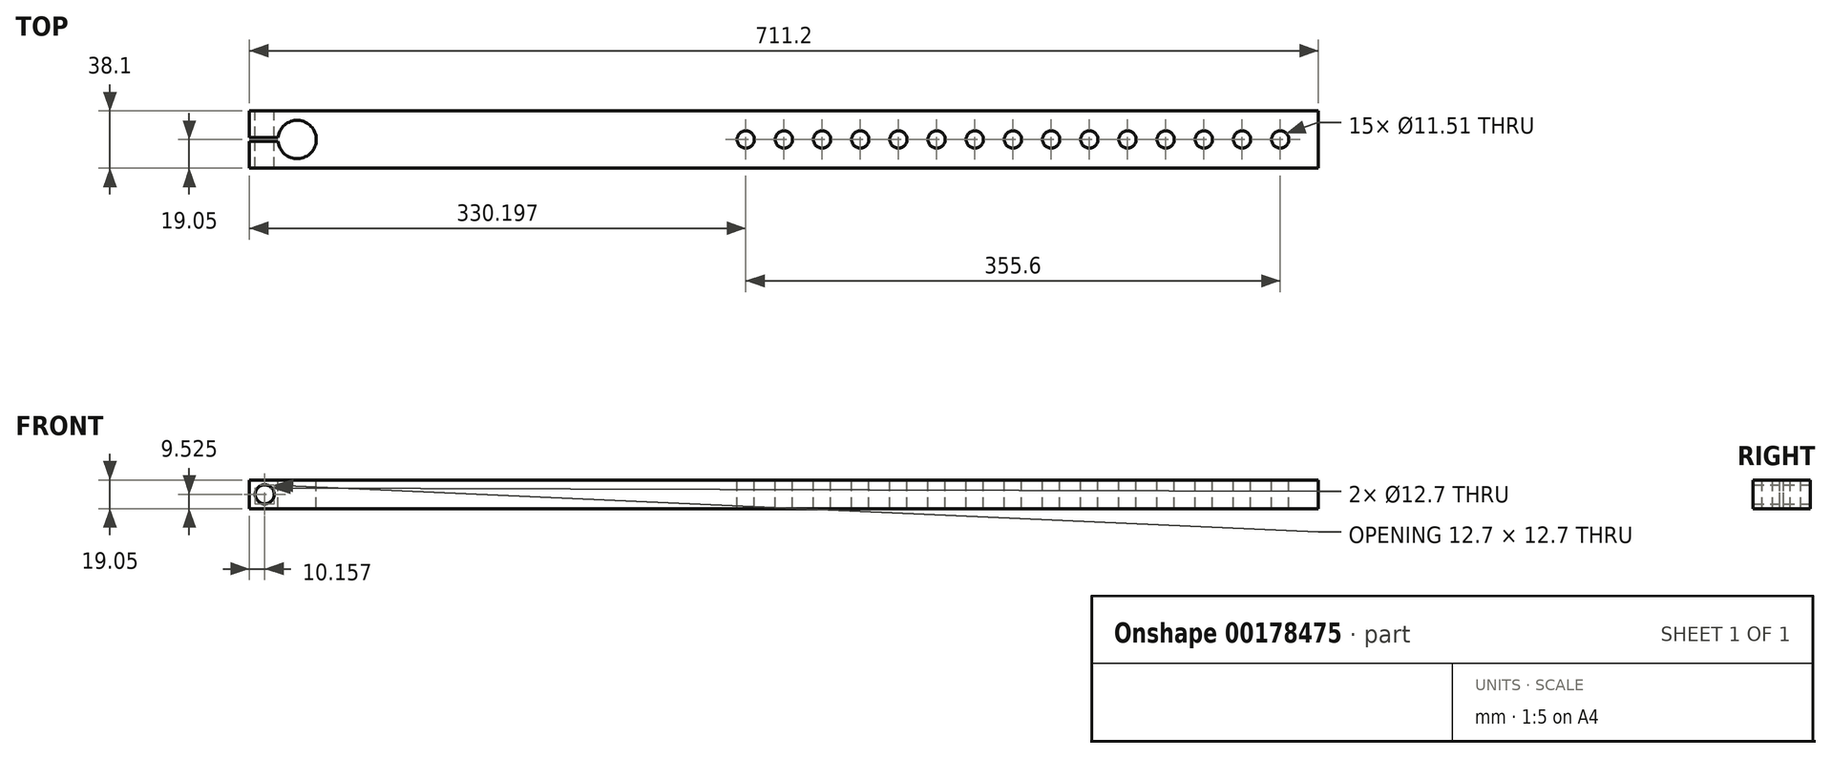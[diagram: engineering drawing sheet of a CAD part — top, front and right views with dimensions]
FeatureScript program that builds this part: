
annotation { "Feature Type Name" : "Feature", "Feature Type Description" : "" }
export const myFeature = defineFeature(function(context is Context, id is Id, definition is map)
    precondition{}
    {
        {
            var Q0;
            Q0=qCreatedBy(makeId("Top.planeOp"),FACE);
            var sketch = newSketch(context, id + "F0", { "sketchPlane" : qUnion([Q0])});
            skLineSegment(sketch, "E0.bottom", {"start": v(-524.1, -19.05) * mm, "end": v(187.1, -19.05) * mm});
            skLineSegment(sketch, "E0.top", {"start": v(-524.1, 19.05) * mm, "end": v(187.1, 19.05) * mm});
            skLineSegment(sketch, "E0.left", {"start": v(-524.1, -19.05) * mm, "end": v(-524.1, 19.05) * mm});
            skLineSegment(sketch, "E0.right", {"start": v(187.1, -19.05) * mm, "end": v(187.1, 19.05) * mm});
            skSolve(sketch);
        }
        {
            var Q0;
            Q0=makeQuery(id+"F0.imprint","IMPRINT",FACE,{"disambiguationData":[TD([[makeQuery(id+"F0.imprint","IMPRINT",EDGE,{"derivedFrom":sQuery(id+"F0.wireOp",EDGE,"E0.bottom")}),1.0]])]});
            extrude(context, id + "F1", {"entities" : qUnion([Q0]), "depth" : 19.05 * mm});
        }
        {
            var Q0;
            Q0=makeQuery(id+"F1.opExtrude","CAP_FACE",FACE,{"disambiguationData":[OSD([sQuery(id+"F0.wireOp",EDGE,"E0.bottom"),sQuery(id+"F0.wireOp",EDGE,"E0.top"),sQuery(id+"F0.wireOp",EDGE,"E0.left"),sQuery(id+"F0.wireOp",EDGE,"E0.right")])],"isStart":false});
            var sketch = newSketch(context, id + "F2", { "sketchPlane" : qUnion([Q0])});
            skLineSegment(sketch, "E1", {"start": v(-524.1, 0) * mm, "end": v(187.1, 0) * mm, "construction": true});
            skPoint(sketch, "E1.endSnap0", {"position": v(-524.1, 0) * mm});
            skPoint(sketch, "E2", {"position": v(-143.1, 0) * mm});
            skPoint(sketch, "E3", {"position": v(-117.7, 0) * mm});
            skPoint(sketch, "E4", {"position": v(-92.3, 0) * mm});
            skPoint(sketch, "E5", {"position": v(-66.9, 0) * mm});
            skPoint(sketch, "E6", {"position": v(-41.5, 0) * mm});
            skPoint(sketch, "E7", {"position": v(-16.1, 0) * mm});
            skPoint(sketch, "E8", {"position": v(9.3, 0) * mm});
            skPoint(sketch, "E9", {"position": v(34.7, 0) * mm});
            skPoint(sketch, "E10", {"position": v(60.1, 0) * mm});
            skPoint(sketch, "E11", {"position": v(85.5, 0) * mm});
            skPoint(sketch, "E12", {"position": v(110.9, 0) * mm});
            skPoint(sketch, "E13", {"position": v(136.3, 0) * mm});
            skPoint(sketch, "E14", {"position": v(161.7, 0) * mm});
            skPoint(sketch, "E15", {"position": v(-168.5, 0) * mm});
            skPoint(sketch, "E16", {"position": v(-193.9, 0) * mm});
            skSolve(sketch);
        }
        {
            var Q0;
            Q0=sQuery(id+"F2.wireOp",VERTEX,"E2");
            var Q1;
            Q1=sQuery(id+"F2.wireOp",VERTEX,"E3");
            var Q2;
            Q2=sQuery(id+"F2.wireOp",VERTEX,"E4");
            var Q3;
            Q3=sQuery(id+"F2.wireOp",VERTEX,"E5");
            var Q4;
            Q4=sQuery(id+"F2.wireOp",VERTEX,"E7");
            var Q5;
            Q5=sQuery(id+"F2.wireOp",VERTEX,"E6");
            var Q6;
            Q6=sQuery(id+"F2.wireOp",VERTEX,"E8");
            var Q7;
            Q7=sQuery(id+"F2.wireOp",VERTEX,"E9");
            var Q8;
            Q8=sQuery(id+"F2.wireOp",VERTEX,"E10");
            var Q9;
            Q9=sQuery(id+"F2.wireOp",VERTEX,"E11");
            var Q10;
            Q10=sQuery(id+"F2.wireOp",VERTEX,"E15");
            var Q11;
            Q11=sQuery(id+"F2.wireOp",VERTEX,"E16");
            var Q12;
            Q12=sQuery(id+"F2.wireOp",VERTEX,"E12");
            var Q13;
            Q13=sQuery(id+"F2.wireOp",VERTEX,"E13");
            var Q14;
            Q14=sQuery(id+"F2.wireOp",VERTEX,"E14");
            var Q15;
            Q15=makeQuery(id+"F1.opExtrude","SWEPT_BODY",BODY,{"disambiguationData":[OSD([sQuery(id+"F0.wireOp",EDGE,"E0.bottom"),sQuery(id+"F0.wireOp",EDGE,"E0.top"),sQuery(id+"F0.wireOp",EDGE,"E0.left"),sQuery(id+"F0.wireOp",EDGE,"E0.right")])]});
            hole(context, id + "F3", {"style" : HoleStyle.SIMPLE, "endStyle" : HoleEndStyle.THROUGH, "standardTappedOrClearance" : lookupTablePath({ "standard" : "ANSI", "engagement" : "75%", "pitch" : "20 tpi", "size" : "1/2", "type" : "Tapped" }), "standardBlindInLast" : lookupTablePath({ "standard" : "ANSI", "engagement" : "75%", "pitch" : "20 tpi", "size" : "1/2", "type" : "Tapped" }), "holeDiameter" : 11.5 * mm, "locations" : qUnion([Q0, Q1, Q2, Q3, Q4, Q5, Q6, Q7, Q8, Q9, Q10, Q11, Q12, Q13, Q14]), "scope" : qUnion([Q15]), "isTappedThrough" : true, "majorDiameter" : 12.7 * mm, "showTappedDepth" : true});
        }
        {
            var Q0;
            Q0=makeQuery(id+"F1.opExtrude","CAP_FACE",FACE,{"disambiguationData":[OSD([sQuery(id+"F0.wireOp",EDGE,"E0.bottom"),sQuery(id+"F0.wireOp",EDGE,"E0.top"),sQuery(id+"F0.wireOp",EDGE,"E0.left"),sQuery(id+"F0.wireOp",EDGE,"E0.right")])],"isStart":false});
            var sketch = newSketch(context, id + "F4", { "sketchPlane" : qUnion([Q0])});
            skPoint(sketch, "E17", {"position": v(-492.35, 0) * mm});
            skSolve(sketch);
        }
        {
            var Q0;
            Q0=sQuery(id+"F4.wireOp",VERTEX,"E17");
            var Q1;
            Q1=makeQuery(id+"F1.opExtrude","SWEPT_BODY",BODY,{"disambiguationData":[OSD([sQuery(id+"F0.wireOp",EDGE,"E0.bottom"),sQuery(id+"F0.wireOp",EDGE,"E0.top"),sQuery(id+"F0.wireOp",EDGE,"E0.left"),sQuery(id+"F0.wireOp",EDGE,"E0.right")])]});
            hole(context, id + "F5", {"style" : HoleStyle.SIMPLE, "endStyle" : HoleEndStyle.THROUGH, "holeDiameter" : 25.45 * mm, "locations" : qUnion([Q0]), "scope" : qUnion([Q1]), "isTappedThrough" : true});
        }
        {
            var Q0;
            Q0=makeQuery(id+"F1.opExtrude","CAP_FACE",FACE,{"disambiguationData":[OSD([sQuery(id+"F0.wireOp",EDGE,"E0.bottom"),sQuery(id+"F0.wireOp",EDGE,"E0.top"),sQuery(id+"F0.wireOp",EDGE,"E0.left"),sQuery(id+"F0.wireOp",EDGE,"E0.right")])],"isStart":false});
            var sketch = newSketch(context, id + "F6", { "sketchPlane" : qUnion([Q0])});
            skLineSegment(sketch, "E18.bottom", {"start": v(-530.66, 1.27) * mm, "end": v(-494.2, 1.27) * mm});
            skLineSegment(sketch, "E18.top", {"start": v(-530.66, -1.27) * mm, "end": v(-494.2, -1.27) * mm});
            skLineSegment(sketch, "E18.left", {"start": v(-530.66, 1.27) * mm, "end": v(-530.66, -1.27) * mm});
            skLineSegment(sketch, "E18.right", {"start": v(-494.2, 1.27) * mm, "end": v(-494.2, -1.27) * mm});
            skLineSegment(sketch, "E19", {"start": v(-530.66, 0) * mm, "end": v(-524.1, 0) * mm, "construction": true});
            skSolve(sketch);
        }
        {
            var Q0;
            {var subQ0=sQuery(id+"F6.wireOp",EDGE,"E18.left");Q0=makeQuery(id+"F6.imprint","IMPRINT",FACE,{"disambiguationData":[TD([[makeQuery(id+"F6.imprint","IMPRINT",EDGE,{"derivedFrom":subQ0}),1.0]])]});}
            var Q1;
            {var subQ0=sQuery(id+"F6.wireOp",EDGE,"E18.right");Q1=makeQuery(id+"F6.imprint","IMPRINT",FACE,{"disambiguationData":[TD([[makeQuery(id+"F6.imprint","IMPRINT",EDGE,{"derivedFrom":subQ0}),-1.0]])]});}
            var Q2;
            {var subQ0=sQuery(id+"F6.wireOp",EDGE,"E18.bottom");var subQ1=makeQuery(id+"F1.opExtrude","CAP_EDGE",EDGE,{"disambiguationData":[OSD([sQuery(id+"F0.wireOp",EDGE,"E0.left")])],"isStart":false});var subQ2=makeQuery(id+"F6.imprint","INTERSECT",VERTEX,{"derivedFrom":[subQ1,subQ0]});Q2=makeQuery(id+"F6.imprint","IMPRINT",FACE,{"disambiguationData":[TD([[makeQuery(id+"F6.imprint","IMPRINT",EDGE,{"disambiguationData":[TD([[subQ2,1.0]])],"derivedFrom":subQ1}),-1.0]])]});}
            extrude(context, id + "F7", {"entities" : qUnion([Q0, Q1, Q2]), "operationType" : NewBodyOperationType.REMOVE, "endBound" : BoundingType.THROUGH_ALL, "oppositeDirection" : true, "depth" : 25.4 * mm});
        }
        {
            var Q0;
            Q0=makeQuery(id+"F1.opExtrude","SWEPT_FACE",FACE,{"disambiguationData":[OSD([sQuery(id+"F0.wireOp",EDGE,"E0.top")])]});
            var sketch = newSketch(context, id + "F8", { "sketchPlane" : qUnion([Q0])});
            skPoint(sketch, "E20", {"position": v(513.94, 9.53) * mm});
            skLineSegment(sketch, "E21", {"start": v(524.1, 9.53) * mm, "end": v(513.94, 9.53) * mm, "construction": true});
            skSolve(sketch);
        }
        {
            var Q0;
            Q0=sQuery(id+"F8.wireOp",VERTEX,"E20");
            var Q1;
            Q1=makeQuery(id+"F1.opExtrude","SWEPT_BODY",BODY,{"disambiguationData":[OSD([sQuery(id+"F0.wireOp",EDGE,"E0.bottom"),sQuery(id+"F0.wireOp",EDGE,"E0.top"),sQuery(id+"F0.wireOp",EDGE,"E0.left"),sQuery(id+"F0.wireOp",EDGE,"E0.right")])]});
            hole(context, id + "F9", {"style" : HoleStyle.SIMPLE, "endStyle" : HoleEndStyle.THROUGH, "holeDiameter" : 12.7 * mm, "locations" : qUnion([Q0]), "scope" : qUnion([Q1]), "isTappedThrough" : true});
        }
    });
